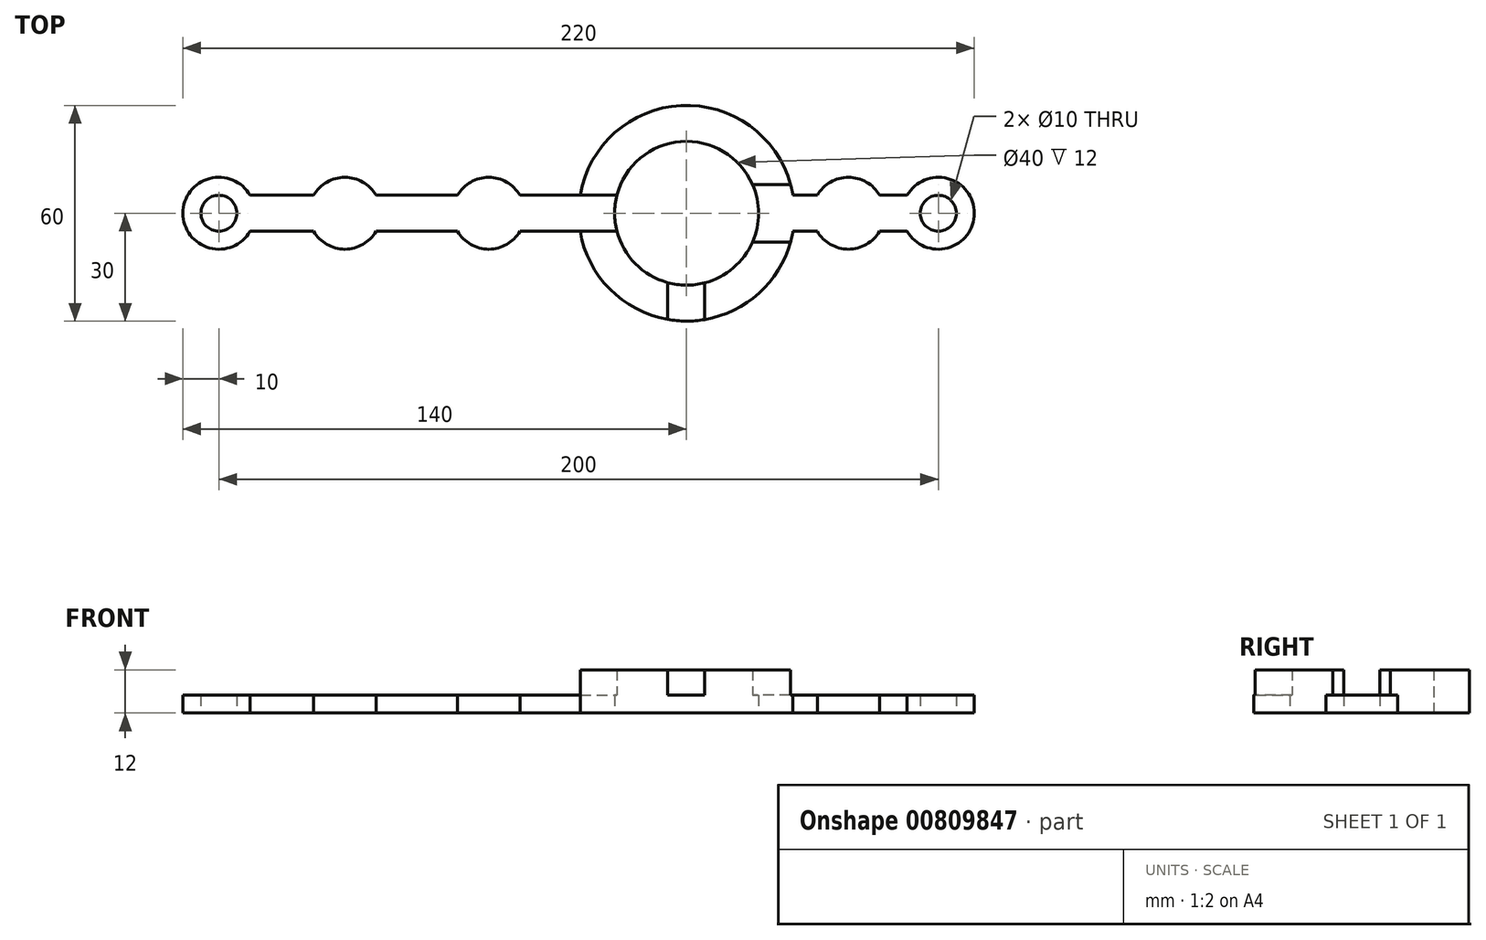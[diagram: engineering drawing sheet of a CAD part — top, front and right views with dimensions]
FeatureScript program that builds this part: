
annotation { "Feature Type Name" : "Feature", "Feature Type Description" : "" }
export const myFeature = defineFeature(function(context is Context, id is Id, definition is map)
    precondition{}
    {
        {
            var Q0;
            Q0=qCreatedBy(makeId("Top.planeOp"),FACE);
            var sketch = newSketch(context, id + "F0", { "sketchPlane" : qUnion([Q0])});
            skCircle(sketch, "E0", {"center": v(0, 0) * mm, "radius": 5 * mm});
            skCircle(sketch, "E1", {"center": v(0, 0) * mm, "radius": 10 * mm});
            skLineSegment(sketch, "E2.bottom", {"start": v(0, 5) * mm, "end": v(-200, 5) * mm});
            skLineSegment(sketch, "E2.top", {"start": v(0, -5) * mm, "end": v(-200, -5) * mm});
            skLineSegment(sketch, "E2.left", {"start": v(0, 5) * mm, "end": v(0, -5) * mm});
            skLineSegment(sketch, "E2.right", {"start": v(-200, 5) * mm, "end": v(-200, -5) * mm});
            skCircle(sketch, "E3", {"center": v(-200, 0) * mm, "radius": 5 * mm});
            skCircle(sketch, "E4", {"center": v(-200, 0) * mm, "radius": 10 * mm});
            skCircle(sketch, "E5", {"center": v(-70, 0) * mm, "radius": 30 * mm});
            skCircle(sketch, "E6", {"center": v(-70, 0) * mm, "radius": 20 * mm});
            skCircle(sketch, "E7", {"center": v(-125, 0) * mm, "radius": 10 * mm});
            skCircle(sketch, "E8", {"center": v(-165, 0) * mm, "radius": 10 * mm});
            skCircle(sketch, "E9", {"center": v(-25, 0) * mm, "radius": 10 * mm});
            skSolve(sketch);
        }
        {
            var Q0;
            Q0 = qSketchRegion(id + "F0", true);
            extrude(context, id + "F1", {"entities" : qUnion([Q0]), "depth" : 5 * mm, "offsetDistance" : 25 * mm});
        }
        {
            var Q0;
            Q0=makeQuery(id+"F1.opExtrude","CAP_FACE",FACE,{"disambiguationData":[OSD([sQuery(id+"F0.wireOp",EDGE,"E0"),sQuery(id+"F0.wireOp",EDGE,"E1"),sQuery(id+"F0.wireOp",EDGE,"E2.bottom"),sQuery(id+"F0.wireOp",EDGE,"E2.top"),sQuery(id+"F0.wireOp",EDGE,"E3"),sQuery(id+"F0.wireOp",EDGE,"E4"),sQuery(id+"F0.wireOp",EDGE,"E5"),sQuery(id+"F0.wireOp",EDGE,"E6")])],"isStart":false});
            var sketch = newSketch(context, id + "F2", { "sketchPlane" : qUnion([Q0])});
            skArc(sketch, "E10", {"start": v(-89.36, -5) * mm, "mid": v(-84.26, -14.03) * mm, "end": v(-75.31, -19.28) * mm});
            skPoint(sketch, "E10.first.point", {"position": v(-68.04, -19.9) * mm});
            skPoint(sketch, "E10.second.point", {"position": v(-87.7, -9.33) * mm});
            skPoint(sketch, "E10.third.point", {"position": v(-59.06, 16.74) * mm});
            skArc(sketch, "E11", {"start": v(-99.58, -5) * mm, "mid": v(-91.33, -21.1) * mm, "end": v(-75.31, -29.53) * mm});
            skPoint(sketch, "E11.first.point", {"position": v(-99.58, 5) * mm});
            skPoint(sketch, "E11.second.point", {"position": v(-40.42, 5) * mm});
            skPoint(sketch, "E11.third.point", {"position": v(-40.42, -5) * mm});
            skLineSegment(sketch, "E12", {"start": v(-99.58, 5) * mm, "end": v(-89.36, 5) * mm});
            skLineSegment(sketch, "E13", {"start": v(-99.58, -5) * mm, "end": v(-89.36, -5) * mm});
            skLineSegment(sketch, "E14", {"start": v(-51.67, 8) * mm, "end": v(-41.09, 8) * mm});
            skLineSegment(sketch, "E15", {"start": v(-41.09, -8) * mm, "end": v(-51.67, -8) * mm});
            skArc(sketch, "E16.trimOffspring", {"start": v(-51.67, 8) * mm, "mid": v(-71.59, 19.94) * mm, "end": v(-89.36, 5) * mm});
            skArc(sketch, "E17.trimOffspring", {"start": v(-41.09, 8) * mm, "mid": v(-71.54, 29.96) * mm, "end": v(-99.58, 5) * mm});
            skPoint(sketch, "E18.orphan", {"position": v(-59.06, -8) * mm});
            skPoint(sketch, "E19.start.orphan", {"position": v(-59.06, 0) * mm});
            skLineSegment(sketch, "E20", {"start": v(-64.93, -19.35) * mm, "end": v(-64.93, -29.57) * mm});
            skLineSegment(sketch, "E21", {"start": v(-75.31, -29.53) * mm, "end": v(-75.31, -19.28) * mm});
            skArc(sketch, "E22.trimOffspring", {"start": v(-64.93, -19.35) * mm, "mid": v(-57, -15.2) * mm, "end": v(-51.67, -8) * mm});
            skArc(sketch, "E23.trimOffspring", {"start": v(-64.93, -29.57) * mm, "mid": v(-49.87, -22.25) * mm, "end": v(-41.09, -8) * mm});
            skPoint(sketch, "E24.start.orphan", {"position": v(-70, -14.19) * mm});
            skSolve(sketch);
        }
        {
            var Q0;
            Q0 = qSketchRegion(id + "F2", true);
            extrude(context, id + "F3", {"entities" : qUnion([Q0]), "operationType" : NewBodyOperationType.ADD, "depth" : 7 * mm, "offsetDistance" : 25 * mm});
        }
    });
